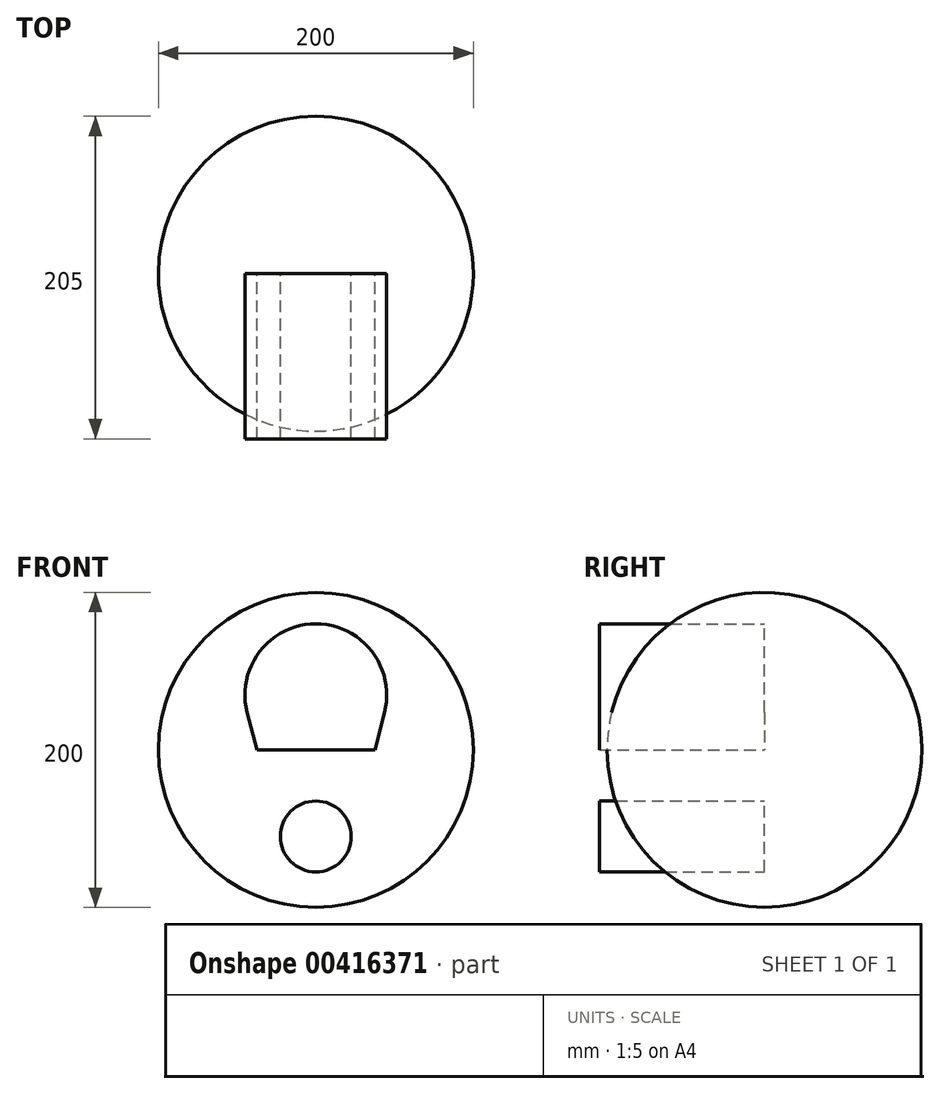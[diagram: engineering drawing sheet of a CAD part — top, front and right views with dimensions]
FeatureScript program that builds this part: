
annotation { "Feature Type Name" : "Feature", "Feature Type Description" : "" }
export const myFeature = defineFeature(function(context is Context, id is Id, definition is map)
    precondition{}
    {
        {
            var Q0;
            Q0=qCreatedBy(makeId("Front.planeOp"),FACE);
            var sketch = newSketch(context, id + "F0", { "sketchPlane" : qUnion([Q0])});
            skCircle(sketch, "E0", {"center": v(0, 0) * mm, "radius": 45 * mm});
            skCircle(sketch, "E1", {"center": v(0, -90) * mm, "radius": 22.5 * mm});
            skLineSegment(sketch, "E2", {"start": v(43.57, -11.25) * mm, "end": v(21.79, -95.62) * mm});
            skLineSegment(sketch, "E3", {"start": v(-21.79, -95.62) * mm, "end": v(-43.57, -11.25) * mm});
            skLineSegment(sketch, "E4", {"start": v(0, 0) * mm, "end": v(0, -90) * mm, "construction": true});
            skLineSegment(sketch, "E5", {"start": v(0, 0) * mm, "end": v(0, -35) * mm, "construction": true});
            skCircle(sketch, "E6", {"center": v(0, -35) * mm, "radius": 100 * mm});
            skLineSegment(sketch, "E7", {"start": v(100, -35) * mm, "end": v(-100, -35) * mm});
            skSolve(sketch);
        }
        {
            var Q0;
            {var subQ5=sQuery(id+"F0.wireOp",EDGE,"E0");var subQ8=sQuery(id+"F0.wireOp",EDGE,"E2");var subQ9=makeQuery(id+"F0.imprint","INTERSECT",VERTEX,{"derivedFrom":[subQ5,subQ8]});Q0=makeQuery(id+"F0.imprint","IMPRINT",FACE,{"disambiguationData":[TD([[makeQuery(id+"F0.imprint","IMPRINT",EDGE,{"disambiguationData":[TD([[subQ9,-1.0]])],"derivedFrom":subQ5}),-1.0]])]});}
            var Q1;
            {var subQ0=sQuery(id+"F0.wireOp",EDGE,"E0");var subQ1=makeQuery(id+"F0.imprint","INTERSECT",VERTEX,{"derivedFrom":[subQ0,sQuery(id+"F0.wireOp",EDGE,"E3")]});Q1=makeQuery(id+"F0.imprint","IMPRINT",FACE,{"disambiguationData":[TD([[makeQuery(id+"F0.imprint","IMPRINT",EDGE,{"disambiguationData":[TD([[subQ1,-1.0]])],"derivedFrom":subQ0}),1.0]])]});}
            var Q2;
            {var subQ0=sQuery(id+"F0.wireOp",EDGE,"E3");var subQ1=sQuery(id+"F0.wireOp",EDGE,"E0");var subQ2=makeQuery(id+"F0.imprint","INTERSECT",VERTEX,{"derivedFrom":[subQ1,subQ0]});Q2=makeQuery(id+"F0.imprint","IMPRINT",FACE,{"disambiguationData":[TD([[makeQuery(id+"F0.imprint","IMPRINT",EDGE,{"disambiguationData":[TD([[subQ2,-1.0]])],"derivedFrom":subQ1}),-1.0]])]});}
            var Q3;
            {var subQ0=sQuery(id+"F0.wireOp",EDGE,"E2");var subQ1=sQuery(id+"F0.wireOp",EDGE,"E0");var subQ2=makeQuery(id+"F0.imprint","INTERSECT",VERTEX,{"derivedFrom":[subQ1,subQ0]});Q3=makeQuery(id+"F0.imprint","IMPRINT",FACE,{"disambiguationData":[TD([[makeQuery(id+"F0.imprint","IMPRINT",EDGE,{"disambiguationData":[TD([[subQ2,1.0]])],"derivedFrom":subQ1}),-1.0]])]});}
            var Q4;
            Q4=sQuery(id+"F0.wireOp",EDGE,"E7");
            revolve(context, id + "F1", {"entities" : qUnion([Q0, Q1, Q2, Q3]), "axis" : qUnion([Q4]), "revolveType" : RevolveType.FULL});
        }
        {
            var Q0;
            {var subQ0=sQuery(id+"F0.wireOp",EDGE,"E0");var subQ1=makeQuery(id+"F0.imprint","INTERSECT",VERTEX,{"derivedFrom":[subQ0,sQuery(id+"F0.wireOp",EDGE,"E3")]});Q0=makeQuery(id+"F0.imprint","IMPRINT",FACE,{"disambiguationData":[TD([[makeQuery(id+"F0.imprint","IMPRINT",EDGE,{"disambiguationData":[TD([[subQ1,-1.0]])],"derivedFrom":subQ0}),1.0]])]});}
            var Q1;
            {var subQ0=sQuery(id+"F0.wireOp",EDGE,"E3");var subQ1=sQuery(id+"F0.wireOp",EDGE,"E0");var subQ2=makeQuery(id+"F0.imprint","INTERSECT",VERTEX,{"derivedFrom":[subQ1,subQ0]});Q1=makeQuery(id+"F0.imprint","IMPRINT",FACE,{"disambiguationData":[TD([[makeQuery(id+"F0.imprint","IMPRINT",EDGE,{"disambiguationData":[TD([[subQ2,-1.0]])],"derivedFrom":subQ1}),-1.0]])]});}
            var Q2;
            {var subQ3=sQuery(id+"F0.wireOp",EDGE,"E7");var subQ8=sQuery(id+"F0.wireOp",EDGE,"E0");var subQ9=makeQuery(id+"F0.imprint","INTERSECT",VERTEX,{"disambiguationData":[OD(0.0)],"derivedFrom":[subQ8,subQ3]});Q2=makeQuery(id+"F0.imprint","IMPRINT",FACE,{"disambiguationData":[TD([[makeQuery(id+"F0.imprint","IMPRINT",EDGE,{"disambiguationData":[TD([[subQ9,-1.0]])],"derivedFrom":subQ8}),-1.0]])]});}
            var Q3;
            {var subQ0=sQuery(id+"F0.wireOp",EDGE,"E7");var subQ1=sQuery(id+"F0.wireOp",EDGE,"E0");var subQ2=makeQuery(id+"F0.imprint","INTERSECT",VERTEX,{"disambiguationData":[OD(0.0)],"derivedFrom":[subQ1,subQ0]});Q3=makeQuery(id+"F0.imprint","IMPRINT",FACE,{"disambiguationData":[TD([[makeQuery(id+"F0.imprint","IMPRINT",EDGE,{"disambiguationData":[TD([[subQ2,-1.0]])],"derivedFrom":subQ1}),1.0]])]});}
            var Q4;
            {var subQ0=sQuery(id+"F0.wireOp",EDGE,"E2");var subQ1=sQuery(id+"F0.wireOp",EDGE,"E0");var subQ2=makeQuery(id+"F0.imprint","INTERSECT",VERTEX,{"derivedFrom":[subQ1,subQ0]});Q4=makeQuery(id+"F0.imprint","IMPRINT",FACE,{"disambiguationData":[TD([[makeQuery(id+"F0.imprint","IMPRINT",EDGE,{"disambiguationData":[TD([[subQ2,1.0]])],"derivedFrom":subQ1}),-1.0]])]});}
            var Q5;
            {var subQ0=sQuery(id+"F0.wireOp",EDGE,"E1");var subQ1=makeQuery(id+"F0.imprint","INTERSECT",VERTEX,{"derivedFrom":[subQ0,sQuery(id+"F0.wireOp",EDGE,"E2")]});Q5=makeQuery(id+"F0.imprint","IMPRINT",FACE,{"disambiguationData":[TD([[makeQuery(id+"F0.imprint","IMPRINT",EDGE,{"disambiguationData":[TD([[subQ1,1.0]])],"derivedFrom":subQ0}),1.0]])]});}
            extrude(context, id + "F2", {"entities" : qUnion([Q0, Q1, Q2, Q3, Q4, Q5]), "depth" : 105 * mm});
        }
    });
